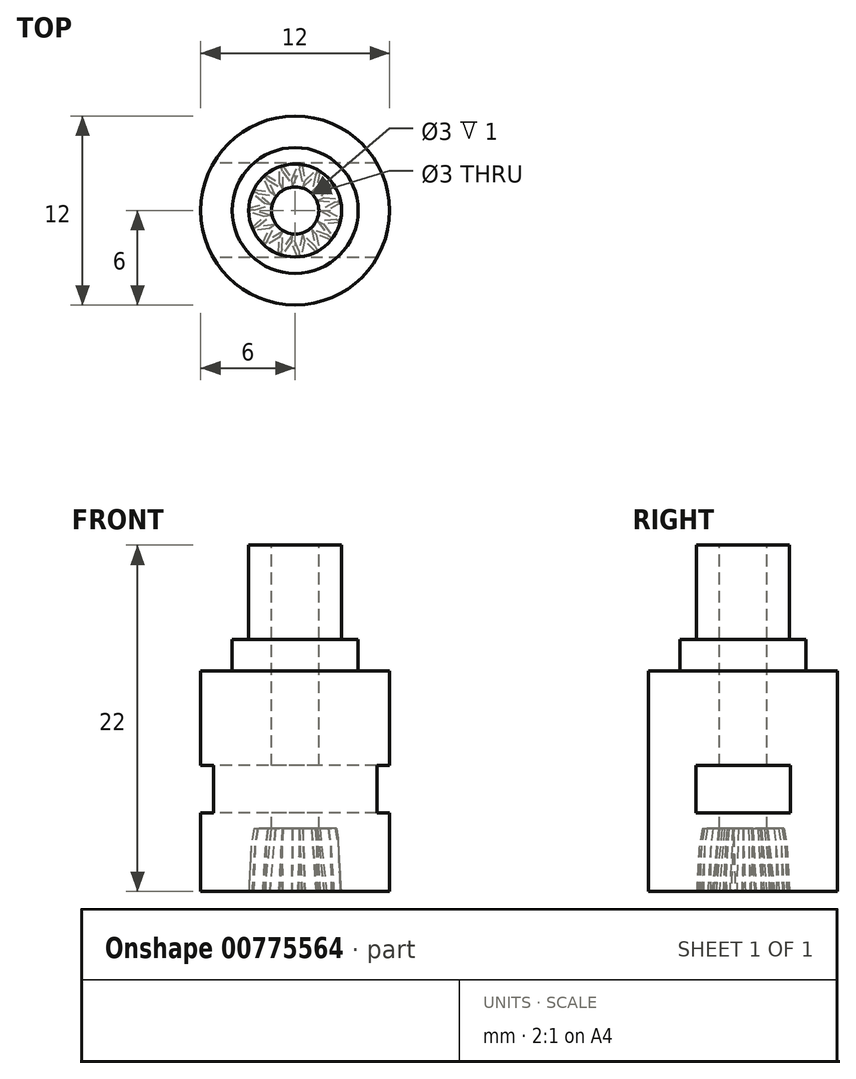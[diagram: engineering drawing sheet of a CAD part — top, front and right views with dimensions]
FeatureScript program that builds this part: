
annotation { "Feature Type Name" : "Feature", "Feature Type Description" : "" }
export const myFeature = defineFeature(function(context is Context, id is Id, definition is map)
    precondition{}
    {
        {
            var Q0;
            Q0=qCreatedBy(makeId("Top.planeOp"),FACE);
            var sketch = newSketch(context, id + "F0", { "sketchPlane" : qUnion([Q0])});
            skCircle(sketch, "E0", {"center": v(0, 0) * mm, "radius": 6 * mm});
            skSolve(sketch);
        }
        {
            var Q0;
            Q0=makeQuery(id+"F0.imprint","IMPRINT",FACE,{"disambiguationData":[TD([[makeQuery(id+"F0.imprint","IMPRINT",EDGE,{"derivedFrom":sQuery(id+"F0.wireOp",EDGE,"E0")}),1.0]])]});
            extrude(context, id + "F1", {"entities" : qUnion([Q0]), "depth" : 16 * mm, "offsetDistance" : 25 * mm});
        }
        {
            var Q0;
            Q0=makeQuery(id+"F1.opExtrude","CAP_FACE",FACE,{"disambiguationData":[OSD([sQuery(id+"F0.wireOp",EDGE,"E0")])],"isStart":false});
            var sketch = newSketch(context, id + "F2", { "sketchPlane" : qUnion([Q0])});
            skCircle(sketch, "E1", {"center": v(0, 0) * mm, "radius": 2.95 * mm});
            skSolve(sketch);
        }
        {
            var Q0;
            Q0 = qSketchRegion(id + "F2", true);
            extrude(context, id + "F3", {"entities" : qUnion([Q0]), "operationType" : NewBodyOperationType.ADD, "depth" : 6 * mm, "offsetDistance" : 25 * mm});
        }
        {
            var Q0;
            Q0=makeQuery(id+"F1.opExtrude","CAP_FACE",FACE,{"disambiguationData":[OSD([sQuery(id+"F0.wireOp",EDGE,"E0")])],"isStart":true});
            var sketch = newSketch(context, id + "F4", { "sketchPlane" : qUnion([Q0])});
            skCircle(sketch, "E2", {"center": v(0, 0) * mm, "radius": 2.95 * mm});
            skLineSegment(sketch, "E3", {"start": v(2.9, 0.5) * mm, "end": v(2, 0) * mm});
            skLineSegment(sketch, "E4", {"start": v(2, 0) * mm, "end": v(2.9, -0.5) * mm});
            skLineSegment(sketch, "E5.1.0", {"start": v(1.83, -0.81) * mm, "end": v(2.45, -1.64) * mm});
            skLineSegment(sketch, "E5.1.1", {"start": v(2.86, -0.72) * mm, "end": v(1.83, -0.81) * mm});
            skLineSegment(sketch, "E5.2.0", {"start": v(1.34, -1.48) * mm, "end": v(1.58, -2.5) * mm});
            skLineSegment(sketch, "E5.2.1", {"start": v(2.32, -1.82) * mm, "end": v(1.34, -1.48) * mm});
            skLineSegment(sketch, "E5.3.0", {"start": v(0.63, -1.9) * mm, "end": v(0.43, -2.92) * mm});
            skLineSegment(sketch, "E5.3.1", {"start": v(1.38, -2.6) * mm, "end": v(0.63, -1.9) * mm});
            skLineSegment(sketch, "E5.4.0", {"start": v(-0.2, -2) * mm, "end": v(-0.79, -2.84) * mm});
            skLineSegment(sketch, "E5.4.1", {"start": v(0.2, -2.94) * mm, "end": v(-0.2, -2) * mm});
            skLineSegment(sketch, "E5.5.0", {"start": v(-0.99, -1.74) * mm, "end": v(-1.87, -2.28) * mm});
            skLineSegment(sketch, "E5.5.1", {"start": v(-1, -2.77) * mm, "end": v(-0.99, -1.74) * mm});
            skLineSegment(sketch, "E5.6.0", {"start": v(-1.6, -1.19) * mm, "end": v(-2.64, -1.32) * mm});
            skLineSegment(sketch, "E5.6.1", {"start": v(-2.04, -2.13) * mm, "end": v(-1.6, -1.19) * mm});
            skLineSegment(sketch, "E5.7.0", {"start": v(-1.95, -0.43) * mm, "end": v(-2.95, -0.14) * mm});
            skLineSegment(sketch, "E5.7.1", {"start": v(-2.73, -1.12) * mm, "end": v(-1.95, -0.43) * mm});
            skLineSegment(sketch, "E5.8.0", {"start": v(-1.96, 0.4) * mm, "end": v(-2.75, 1.07) * mm});
            skLineSegment(sketch, "E5.8.1", {"start": v(-2.95, 0.09) * mm, "end": v(-1.96, 0.4) * mm});
            skLineSegment(sketch, "E5.9.0", {"start": v(-1.63, 1.16) * mm, "end": v(-2.08, 2.1) * mm});
            skLineSegment(sketch, "E5.9.1", {"start": v(-2.66, 1.27) * mm, "end": v(-1.63, 1.16) * mm});
            skLineSegment(sketch, "E5.10.0", {"start": v(-1.02, 1.72) * mm, "end": v(-1.06, 2.75) * mm});
            skLineSegment(sketch, "E5.10.1", {"start": v(-1.91, 2.24) * mm, "end": v(-1.02, 1.72) * mm});
            skLineSegment(sketch, "E5.11.0", {"start": v(-0.24, 1.99) * mm, "end": v(0.15, 2.95) * mm});
            skLineSegment(sketch, "E5.11.1", {"start": v(-0.84, 2.83) * mm, "end": v(-0.24, 1.99) * mm});
            skLineSegment(sketch, "E5.12.0", {"start": v(0.59, 1.91) * mm, "end": v(1.33, 2.63) * mm});
            skLineSegment(sketch, "E5.12.1", {"start": v(0.38, 2.93) * mm, "end": v(0.59, 1.91) * mm});
            skLineSegment(sketch, "E5.13.0", {"start": v(1.31, 1.5) * mm, "end": v(2.29, 1.86) * mm});
            skLineSegment(sketch, "E5.13.1", {"start": v(1.53, 2.52) * mm, "end": v(1.31, 1.5) * mm});
            skLineSegment(sketch, "E5.14.0", {"start": v(1.81, 0.85) * mm, "end": v(2.85, 0.78) * mm});
            skLineSegment(sketch, "E5.14.1", {"start": v(2.42, 1.68) * mm, "end": v(1.81, 0.85) * mm});
            skLineSegment(sketch, "E5.anchor1", {"start": v(0, 0) * mm, "end": v(2.9, -0.5) * mm, "construction": true});
            skLineSegment(sketch, "E5.anchor2", {"start": v(0, 0) * mm, "end": v(2.85, 0.78) * mm, "construction": true});
            skSolve(sketch);
        }
        {
            var Q0;
            {var subQ3=sQuery(id+"F4.wireOp",EDGE,"E3");Q0=makeQuery(id+"F4.imprint","IMPRINT",FACE,{"disambiguationData":[TD([[makeQuery(id+"F4.imprint","IMPRINT",EDGE,{"derivedFrom":subQ3}),-1.0]])]});}
            extrude(context, id + "F5", {"entities" : qUnion([Q0]), "operationType" : NewBodyOperationType.REMOVE, "oppositeDirection" : true, "depth" : 4 * mm, "offsetDistance" : 25 * mm, "hasDraft" : true, "draftAngle" : 3 * degree, "draftPullDirection" : true});
        }
        {
            var Q0;
            Q0=makeQuery(id+"F3.opExtrude","CAP_FACE",FACE,{"disambiguationData":[OSD([sQuery(id+"F2.wireOp",EDGE,"E1")])],"isStart":false});
            var sketch = newSketch(context, id + "F6", { "sketchPlane" : qUnion([Q0])});
            skCircle(sketch, "E6", {"center": v(0, 0) * mm, "radius": 1.5 * mm});
            skSolve(sketch);
        }
        {
            var Q0;
            Q0 = qSketchRegion(id + "F6", true);
            extrude(context, id + "F7", {"entities" : qUnion([Q0]), "operationType" : NewBodyOperationType.REMOVE, "oppositeDirection" : true, "depth" : 25 * mm, "offsetDistance" : 25 * mm});
        }
        {
            var Q0;
            Q0=makeQuery(id+"F1.opExtrude","CAP_FACE",FACE,{"disambiguationData":[OSD([sQuery(id+"F0.wireOp",EDGE,"E0")])],"isStart":false});
            var sketch = newSketch(context, id + "F8", { "sketchPlane" : qUnion([Q0])});
            skCircle(sketch, "E7", {"center": v(0, 0) * mm, "radius": 4 * mm});
            skSolve(sketch);
        }
        {
            var Q0;
            Q0=makeQuery(id+"F8.imprint","IMPRINT",FACE,{"disambiguationData":[TD([[makeQuery(id+"F8.imprint","IMPRINT",EDGE,{"derivedFrom":sQuery(id+"F8.wireOp",EDGE,"E7")}),-1.0]])]});
            extrude(context, id + "F9", {"entities" : qUnion([Q0]), "operationType" : NewBodyOperationType.REMOVE, "oppositeDirection" : true, "depth" : 2 * mm, "offsetDistance" : 25 * mm});
        }
        {
            var Q0;
            Q0=qCreatedBy(makeId("Right.planeOp"),FACE);
            var sketch = newSketch(context, id + "F10", { "sketchPlane" : qUnion([Q0])});
            skLineSegment(sketch, "E8.bottom", {"start": v(-3, 8) * mm, "end": v(3, 8) * mm});
            skLineSegment(sketch, "E8.top", {"start": v(-3, 5) * mm, "end": v(3, 5) * mm});
            skLineSegment(sketch, "E8.left", {"start": v(-3, 8) * mm, "end": v(-3, 5) * mm});
            skLineSegment(sketch, "E8.right", {"start": v(3, 8) * mm, "end": v(3, 5) * mm});
            skSolve(sketch);
        }
        {
            var Q0;
            Q0 = qSketchRegion(id + "F10", true);
            extrude(context, id + "F11", {"entities" : qUnion([Q0]), "operationType" : NewBodyOperationType.REMOVE, "endBound" : BoundingType.SYMMETRIC, "depth" : 25 * mm, "offsetDistance" : 25 * mm});
        }
    });
